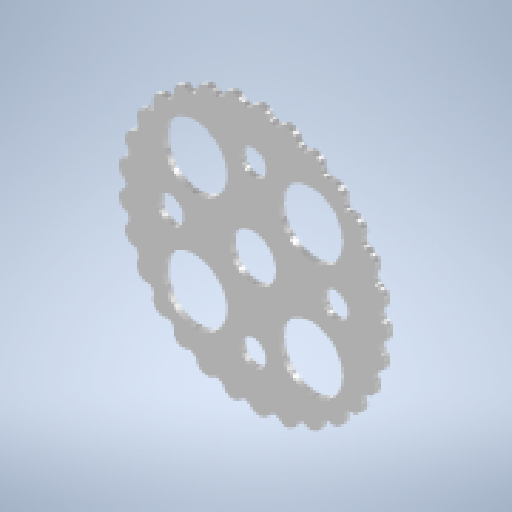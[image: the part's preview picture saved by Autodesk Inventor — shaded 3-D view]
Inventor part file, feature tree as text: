
AUTODESK INVENTOR PART (.ipt)
format: ipt  version: 2024 (Build 280153000, 153)  size: 341,504 bytes
history: native  units: mm
features: sketch x4, extrude x3, other x2, pattern_circular x2, hole x1
ambient origin geometry x8: Origin, YZ Plane, XZ Plane, XY Plane, X Axis, Y Axis, Z Axis, Center Point
bodies: Body1 (feature_tree)
feature tree (12):
  other  "ソリッド1"
  extrude  "押し出し1"  Depth=3600.0mm TaperAngle=0.0deg
  hole  "穴1"  [1 undecoded]
  extrude  "押し出し2"  Depth=14.0mm
  pattern_circular  "円形状パターン1"  [2 undecoded]
  extrude  "押し出し3"  TaperAngle=0.0deg  [1 undecoded]
  pattern_circular  "円形状パターン2"  Count=4 Angle=360.0deg
  sketch  "スケッチ1"
  other  "2D 計算式曲線1"
  sketch  "スケッチ2"
  sketch  "スケッチ3"
  sketch  "スケッチ4"
note: 4 required parameter values undecoded (feature->parameter linkage not recoverable at this tier; creation-order binding heuristic only, values carry confidence <= 0.55)
